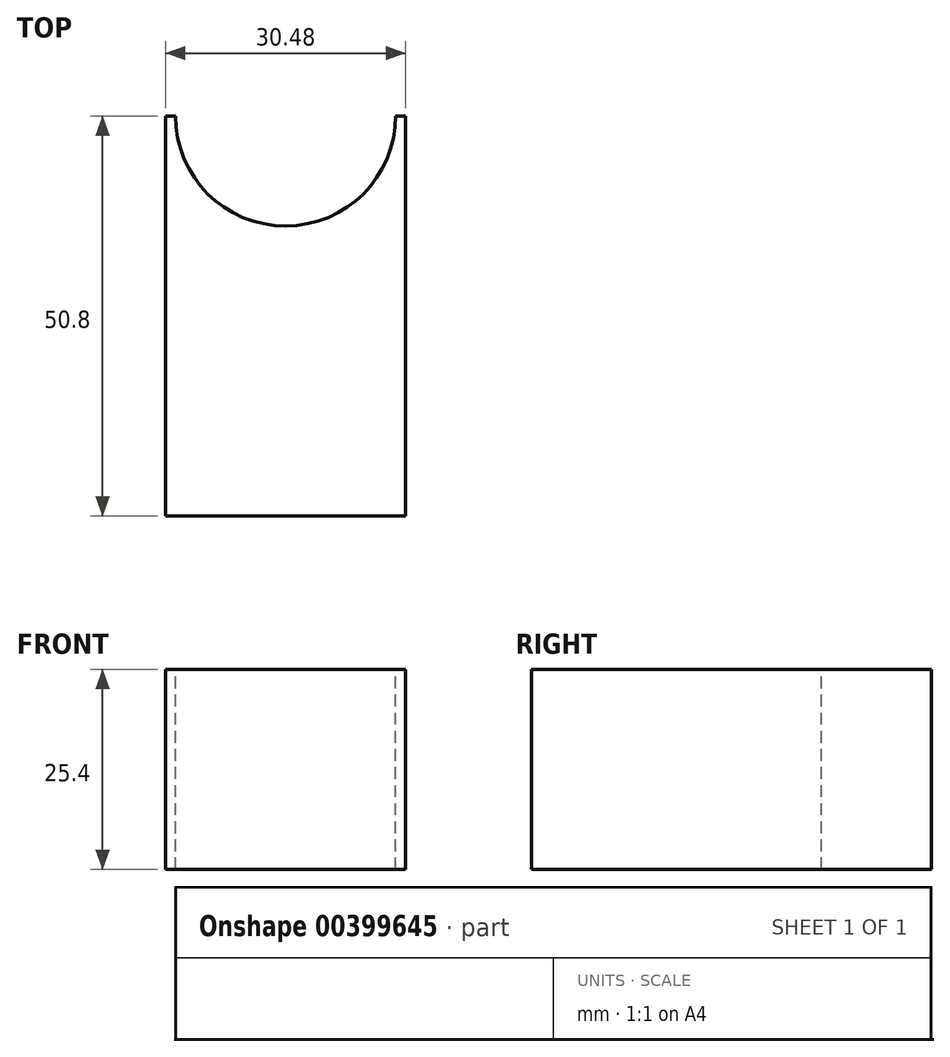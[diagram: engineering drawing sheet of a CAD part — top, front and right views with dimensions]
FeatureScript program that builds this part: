
annotation { "Feature Type Name" : "Feature", "Feature Type Description" : "" }
export const myFeature = defineFeature(function(context is Context, id is Id, definition is map)
    precondition{}
    {
        {
            var Q0;
            Q0=qCreatedBy(makeId("Top.planeOp"),FACE);
            var sketch = newSketch(context, id + "F0", { "sketchPlane" : qUnion([Q0])});
            skLineSegment(sketch, "E0.bottom", {"start": v(-15.24, 0) * mm, "end": v(15.24, 0) * mm});
            skLineSegment(sketch, "E0.top", {"start": v(-15.24, 50.8) * mm, "end": v(15.24, 50.8) * mm});
            skLineSegment(sketch, "E0.left", {"start": v(-15.24, 0) * mm, "end": v(-15.24, 50.8) * mm});
            skLineSegment(sketch, "E0.right", {"start": v(15.24, 0) * mm, "end": v(15.24, 50.8) * mm});
            skSolve(sketch);
        }
        {
            var Q0;
            Q0=makeQuery(id+"F0.imprint","IMPRINT",FACE,{"disambiguationData":[TD([[makeQuery(id+"F0.imprint","IMPRINT",EDGE,{"derivedFrom":sQuery(id+"F0.wireOp",EDGE,"E0.bottom")}),1.0]])]});
            extrude(context, id + "F1", {"entities" : qUnion([Q0]), "depth" : 25.4 * mm});
        }
        {
            var Q0;
            Q0=makeQuery(id+"F1.opExtrude","CAP_FACE",FACE,{"disambiguationData":[OSD([sQuery(id+"F0.wireOp",EDGE,"E0.bottom"),sQuery(id+"F0.wireOp",EDGE,"E0.top"),sQuery(id+"F0.wireOp",EDGE,"E0.left"),sQuery(id+"F0.wireOp",EDGE,"E0.right")])],"isStart":false});
            var sketch = newSketch(context, id + "F2", { "sketchPlane" : qUnion([Q0])});
            skCircle(sketch, "E1", {"center": v(0, 50.8) * mm, "radius": 13.97 * mm});
            skSolve(sketch);
        }
        {
            var Q0;
            {var subQ0=sQuery(id+"F2.wireOp",EDGE,"E1");var subQ1=makeQuery(id+"F1.opExtrude","CAP_EDGE",EDGE,{"disambiguationData":[OSD([sQuery(id+"F0.wireOp",EDGE,"E0.top")])],"isStart":false});var subQ2=makeQuery(id+"F2.imprint","INTERSECT",VERTEX,{"disambiguationData":[OD(0.0)],"derivedFrom":[subQ1,subQ0]});Q0=makeQuery(id+"F2.imprint","IMPRINT",FACE,{"disambiguationData":[TD([[makeQuery(id+"F2.imprint","IMPRINT",EDGE,{"disambiguationData":[TD([[subQ2,-1.0]])],"derivedFrom":subQ0}),1.0]])]});}
            extrude(context, id + "F3", {"entities" : qUnion([Q0]), "operationType" : NewBodyOperationType.REMOVE, "oppositeDirection" : true, "depth" : 25.4 * mm});
        }
    });
